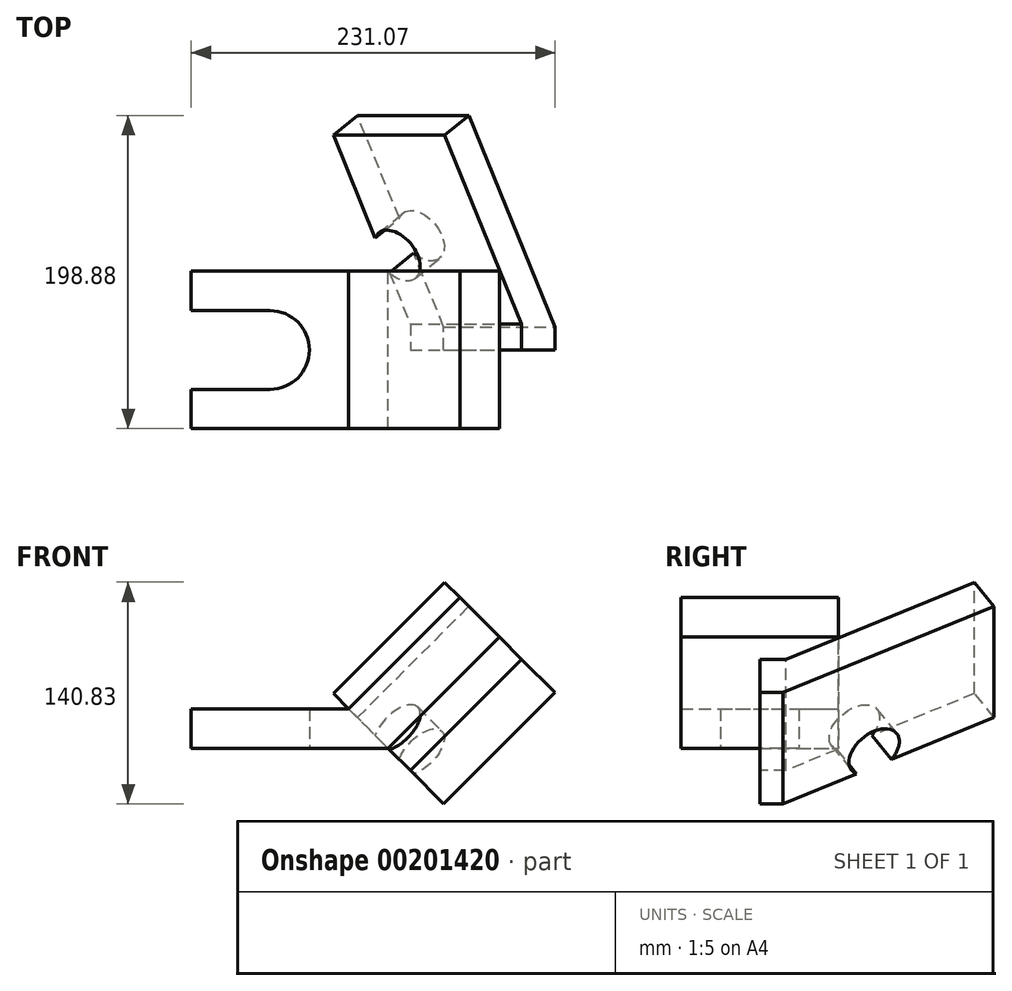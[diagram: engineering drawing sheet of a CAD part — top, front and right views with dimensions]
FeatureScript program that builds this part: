
annotation { "Feature Type Name" : "Feature", "Feature Type Description" : "" }
export const myFeature = defineFeature(function(context is Context, id is Id, definition is map)
    precondition{}
    {
        {
            var Q0;
            Q0=qCreatedBy(makeId("Front.planeOp"),FACE);
            var sketch = newSketch(context, id + "F0", { "sketchPlane" : qUnion([Q0])});
            skLineSegment(sketch, "E0", {"start": v(0, 0) * mm, "end": v(-125, 0) * mm});
            skLineSegment(sketch, "E1", {"start": v(-125, 0) * mm, "end": v(-125, 25) * mm});
            skLineSegment(sketch, "E2", {"start": v(-125, 25) * mm, "end": v(-25, 25) * mm});
            skLineSegment(sketch, "E3", {"start": v(-25, 25) * mm, "end": v(45.71, 95.71) * mm});
            skLineSegment(sketch, "E4", {"start": v(45.71, 95.71) * mm, "end": v(70.71, 70.71) * mm});
            skLineSegment(sketch, "E5", {"start": v(70.71, 70.71) * mm, "end": v(0, 0) * mm});
            skLineSegment(sketch, "E6", {"start": v(-25, 25) * mm, "end": v(0, 0) * mm, "construction": true});
            skSolve(sketch);
        }
        {
            var Q0;
            Q0=makeQuery(id+"F0.imprint","IMPRINT",FACE,{"disambiguationData":[TD([[makeQuery(id+"F0.imprint","IMPRINT",EDGE,{"derivedFrom":sQuery(id+"F0.wireOp",EDGE,"E0")}),-1.0]])]});
            extrude(context, id + "F1", {"entities" : qUnion([Q0]), "endBound" : BoundingType.SYMMETRIC, "depth" : 100 * mm});
        }
        {
            var Q0;
            Q0=makeQuery(id+"F1.opExtrude","SWEPT_FACE",FACE,{"disambiguationData":[OSD([sQuery(id+"F0.wireOp",EDGE,"E4")])]});
            var sketch = newSketch(context, id + "F2", { "sketchPlane" : qUnion([Q0])});
            skLineSegment(sketch, "E7", {"start": v(0, -50) * mm, "end": v(14.64, -50) * mm});
            skLineSegment(sketch, "E8", {"start": v(14.64, -50) * mm, "end": v(148.88, 27.5) * mm});
            skLineSegment(sketch, "E9", {"start": v(148.88, 27.5) * mm, "end": v(136.38, 49.15) * mm});
            skLineSegment(sketch, "E10", {"start": v(136.38, 49.15) * mm, "end": v(16.6, -20) * mm});
            skLineSegment(sketch, "E11", {"start": v(16.6, -20) * mm, "end": v(0, -20) * mm});
            skLineSegment(sketch, "E12", {"start": v(0, -20) * mm, "end": v(0, -50) * mm});
            skSolve(sketch);
        }
        {
            var Q0;
            Q0=makeQuery(id+"F2.imprint","IMPRINT",FACE,{"disambiguationData":[TD([[makeQuery(id+"F2.imprint","IMPRINT",EDGE,{"derivedFrom":sQuery(id+"F2.wireOp",EDGE,"E7")}),1.0]])]});
            var Q1;
            Q1=makeQuery(id+"F1.opExtrude","CAP_VERTEX",VERTEX,{"disambiguationData":[OSD([sQuery(id+"F0.wireOp",EDGE,"E0"),sQuery(id+"F0.wireOp",EDGE,"E5")])],"isStart":false});
            extrude(context, id + "F3", {"entities" : qUnion([Q0]), "operationType" : NewBodyOperationType.ADD, "endBound" : BoundingType.UP_TO_VERTEX, "oppositeDirection" : true, "endBoundEntityVertex" : qUnion([Q1]), "depth" : 25 * mm});
        }
        {
            var Q0;
            Q0=makeQuery(id+"F1.opExtrude","SWEPT_FACE",FACE,{"disambiguationData":[OSD([sQuery(id+"F0.wireOp",EDGE,"E0")])]});
            var sketch = newSketch(context, id + "F4", { "sketchPlane" : qUnion([Q0])});
            skLineSegment(sketch, "E13.bottom", {"start": v(-75, -25) * mm, "end": v(-125, -25) * mm});
            skLineSegment(sketch, "E13.top", {"start": v(-75, 25) * mm, "end": v(-125, 25) * mm});
            skLineSegment(sketch, "E13.left", {"start": v(-75, -25) * mm, "end": v(-75, 25) * mm, "construction": true});
            skLineSegment(sketch, "E13.right", {"start": v(-125, -25) * mm, "end": v(-125, 25) * mm});
            skPoint(sketch, "E13.middle", {"position": v(-100, 0) * mm});
            skPoint(sketch, "E13.middle.positionSnap0", {"position": v(-125, 0) * mm});
            skPoint(sketch, "E13.centerSnap0", {"position": v(-125, 0) * mm});
            skArc(sketch, "E14", {"start": v(-75, 25) * mm, "mid": v(-50, 0) * mm, "end": v(-75, -25) * mm});
            skSolve(sketch);
        }
        {
            var Q0;
            Q0=makeQuery(id+"F4.imprint","IMPRINT",FACE,{"disambiguationData":[TD([[makeQuery(id+"F4.imprint","IMPRINT",EDGE,{"derivedFrom":sQuery(id+"F4.wireOp",EDGE,"E13.bottom")}),-1.0]])]});
            extrude(context, id + "F5", {"entities" : qUnion([Q0]), "operationType" : NewBodyOperationType.REMOVE, "endBound" : BoundingType.THROUGH_ALL, "oppositeDirection" : true, "depth" : 25 * mm});
        }
        {
            var Q0;
            Q0=makeQuery(id+"F3.opExtrude","SWEPT_FACE",FACE,{"disambiguationData":[OSD([sQuery(id+"F2.wireOp",EDGE,"E8")])]});
            var sketch = newSketch(context, id + "F6", { "sketchPlane" : qUnion([Q0])});
            skLineSegment(sketch, "E15", {"start": v(131.2, -75.13) * mm, "end": v(95.2, -33.55) * mm, "construction": true});
            skArc(sketch, "E16", {"start": v(76.3, -49.92) * mm, "mid": v(78.83, -14.65) * mm, "end": v(114.1, -17.18) * mm});
            skLineSegment(sketch, "E17", {"start": v(76.3, -49.92) * mm, "end": v(112.3, -91.5) * mm});
            skLineSegment(sketch, "E18", {"start": v(112.3, -91.5) * mm, "end": v(150.1, -58.76) * mm});
            skLineSegment(sketch, "E19", {"start": v(150.1, -58.76) * mm, "end": v(114.1, -17.18) * mm});
            skCircle(sketch, "E20", {"center": v(54.6, 13.32) * mm, "radius": 18.5 * mm});
            skSolve(sketch);
        }
        {
            var Q0;
            Q0=makeQuery(id+"F6.imprint","IMPRINT",FACE,{"disambiguationData":[TD([[makeQuery(id+"F6.imprint","IMPRINT",EDGE,{"derivedFrom":sQuery(id+"F6.wireOp",EDGE,"E16")}),-1.0]])]});
            var Q1;
            Q1=makeQuery(id+"F6.imprint","IMPRINT",FACE,{"disambiguationData":[TD([[makeQuery(id+"F6.imprint","IMPRINT",EDGE,{"derivedFrom":sQuery(id+"F6.wireOp",EDGE,"E20")}),1.0]])]});
            extrude(context, id + "F7", {"entities" : qUnion([Q0, Q1]), "operationType" : NewBodyOperationType.REMOVE, "endBound" : BoundingType.UP_TO_NEXT, "oppositeDirection" : true, "depth" : 25 * mm});
        }
    });
